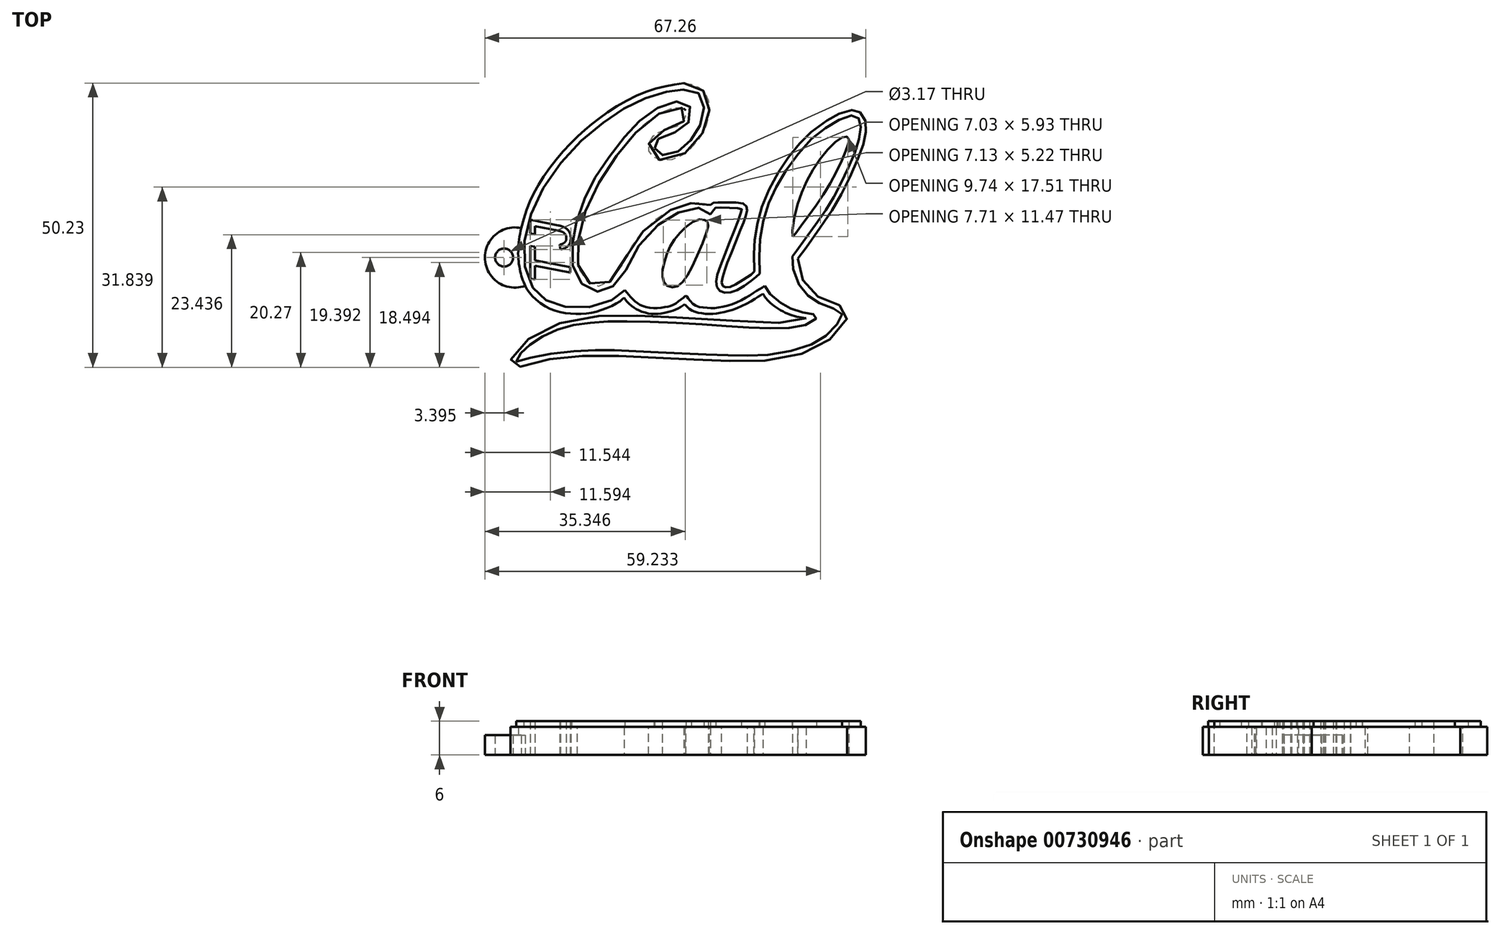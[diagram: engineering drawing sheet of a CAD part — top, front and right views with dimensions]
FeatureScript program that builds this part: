
annotation { "Feature Type Name" : "Feature", "Feature Type Description" : "" }
export const myFeature = defineFeature(function(context is Context, id is Id, definition is map)
    precondition{}
    {
        {
            var Q0;
            Q0=qCreatedBy(makeId("Top.planeOp"),FACE);
            var sketch = newSketch(context, id + "F0", { "sketchPlane" : qUnion([Q0])});
            skFitSpline(sketch, "E0", {"points": [v(-4.7, 24.02) * mm, v(-9.21, 23.15) * mm, v(-14.3, 21.16) * mm, v(-19.5, 17.88) * mm, v(-22.84, 15.12) * mm, v(-26.76, 11.1) * mm, v(-29.99, 6.61) * mm, v(-32.03, 2.73) * mm, v(-33.4, -1.61) * mm, v(-33.93, -5.95) * mm, v(-33.53, -9.41) * mm, v(-32.68, -11.82) * mm, v(-31.5, -13.58) * mm, v(-28.51, -15.76) * mm, v(-25.22, -16.67) * mm, v(-21.85, -16.67) * mm, v(-18.53, -15.85) * mm, v(-15.8, -14.43) * mm, v(-15.24, -13.92) * mm], "startDerivative": vector(-73.34, -11.53) * mm, "endDerivative": vector(17.37, 18.62) * mm});
            skFitSpline(sketch, "E1", {"points": [v(-4.7, 24.02) * mm, v(-3.12, 23.72) * mm, v(-1.32, 22.73) * mm, v(-0.4, 21.1) * mm, v(-0.19, 19.64) * mm, v(-0.46, 17.5) * mm, v(-1.34, 15.24) * mm, v(-3, 12.9) * mm, v(-5.25, 11.12) * mm, v(-8.18, 10.3) * mm, v(-10.22, 11.1) * mm, v(-10.93, 12.5) * mm, v(-10.4, 14.33) * mm, v(-9.18, 15.29) * mm, v(-7.2, 15.98) * mm, v(-5.28, 16.76) * mm, v(-4.46, 17.73) * mm, v(-4.35, 19.05) * mm, v(-4.7, 19.49) * mm, v(-5.77, 19.74) * mm, v(-8.08, 19.08) * mm, v(-10.95, 17.28) * mm, v(-13.73, 14.65) * mm, v(-15.92, 11.97) * mm, v(-18.22, 8.83) * mm, v(-20.42, 5.07) * mm, v(-22.03, 1.43) * mm, v(-22.95, -1.6) * mm, v(-23.43, -5.01) * mm, v(-23.44, -7.42) * mm, v(-22.82, -9.67) * mm, v(-21.67, -11.12) * mm, v(-20.22, -11.83) * mm, v(-18.54, -11.59) * mm, v(-16.3, -9.45) * mm, v(-14.2, -5.42) * mm, v(-12.55, -2.99) * mm, v(-9.6, 0) * mm, v(-5.75, 2.15) * mm, v(-4.7, 2.5) * mm, v(-2.6, 2.9) * mm, v(-0.85, 2.81) * mm, v(0, 2.46) * mm], "startDerivative": vector(77.61, -10.14) * mm, "endDerivative": vector(51.5, -26.92) * mm});
            skFitSpline(sketch, "E2", {"points": [v(0, 2.46) * mm, v(0.28, 2.72) * mm, v(0.87, 2.9) * mm, v(2.4, 2.94) * mm, v(5.4, 2.83) * mm, v(6.2, 2.46) * mm, v(6.5, 1.89) * mm, v(6.5, 1.4) * mm, v(6.07, 0) * mm, v(5.35, -1.82) * mm, v(3.47, -6.54) * mm, v(2.55, -9.02) * mm, v(2.07, -10.65) * mm, v(2.04, -11.5) * mm, v(2.25, -11.9) * mm, v(2.52, -12.02) * mm, v(2.9, -12.1) * mm, v(3.58, -12) * mm, v(5, -11.26) * mm, v(7.38, -9.65) * mm, v(7.75, -9.28) * mm], "startDerivative": vector(8.73, 10) * mm, "endDerivative": vector(7.71, 9.34) * mm});
            skFitSpline(sketch, "E3", {"points": [v(7.75, -9.28) * mm, v(7.67, -6.17) * mm, v(7.75, -4.22) * mm, v(8.16, -1.42) * mm, v(8.86, 1.43) * mm, v(10.07, 4.56) * mm, v(11.9, 8.03) * mm, v(13.77, 10.86) * mm, v(15.67, 13.23) * mm, v(17.5, 15.1) * mm, v(20.59, 17.4) * mm, v(22.34, 18.43) * mm, v(24.19, 19.11) * mm, v(25.4, 19.25) * mm, v(26.1, 19.05) * mm, v(26.66, 18.64) * mm, v(27.28, 17.6) * mm, v(27.44, 16.52) * mm, v(27.4, 15.04) * mm, v(27.06, 13.35) * mm, v(26.43, 11.57) * mm, v(24.97, 8.1) * mm, v(23.3, 4.7) * mm, v(21.54, 1.6) * mm, v(18.9, -2.23) * mm, v(15.96, -6.32) * mm, v(15.47, -6.98) * mm], "startDerivative": vector(-2.8, 76.12) * mm, "endDerivative": vector(-16.99, -22) * mm});
            skFitSpline(sketch, "E4", {"points": [v(15.47, -6.98) * mm, v(15.47, -8.07) * mm, v(15.9, -9.84) * mm, v(16.65, -11.36) * mm, v(17.4, -12.33) * mm, v(18.9, -13.64) * mm, v(20.59, -14.36) * mm, v(22.36, -15.03) * mm, v(23.17, -15.48) * mm, v(23.92, -16.1) * mm, v(24.16, -17.1) * mm, v(24.02, -17.86) * mm, v(23.06, -19.38) * mm, v(20.9, -21.42) * mm, v(18.38, -22.95) * mm, v(15.02, -24.15) * mm, v(10.48, -24.94) * mm, v(6.7, -25.1) * mm, v(2.6, -25.05) * mm, v(-1.8, -24.88) * mm, v(-4.7, -24.77) * mm, v(-10.38, -24.47) * mm, v(-14.79, -24.26) * mm, v(-18.25, -24.15) * mm, v(-22.76, -24.23) * mm, v(-26.47, -24.5) * mm, v(-29.37, -25) * mm, v(-32.67, -25.83) * mm, v(-34.12, -26.19) * mm, v(-34.7, -26.14) * mm, v(-35.17, -25.7) * mm, v(-35.28, -25.12) * mm, v(-34.94, -24.15) * mm, v(-33.62, -22.44) * mm, v(-30.22, -20.02) * mm, v(-26.9, -18.52) * mm, v(-21.96, -17.34) * mm, v(-17.65, -17.1) * mm, v(-12.83, -17.1) * mm, v(-8.42, -17.27) * mm, v(-0.45, -17.68) * mm, v(9.32, -18.29) * mm, v(13.39, -18.32) * mm, v(16.5, -17.78) * mm, v(16.89, -17.55) * mm], "startDerivative": vector(-4.14, -70.71) * mm, "endDerivative": vector(29.82, 23.88) * mm});
            skFitSpline(sketch, "E5", {"points": [v(16.89, -17.55) * mm, v(14.28, -16.98) * mm, v(11.54, -15.58) * mm, v(9.76, -13.96) * mm, v(9.29, -13.24) * mm], "startDerivative": vector(-9.33, 1.49) * mm, "endDerivative": vector(-2.3, 4.22) * mm});
            skFitSpline(sketch, "E6", {"points": [v(9.29, -13.24) * mm, v(8.22, -13.9) * mm, v(4.92, -15.68) * mm, v(2.04, -16.52) * mm, v(0, -16.77) * mm, v(-2.04, -16.59) * mm, v(-3.52, -16.02) * mm, v(-4.42, -15.2) * mm, v(-4.52, -15.03) * mm], "startDerivative": vector(-8.4, -5.18) * mm, "endDerivative": vector(-1.48, 3.32) * mm});
            skFitSpline(sketch, "E7", {"points": [v(-4.52, -15.03) * mm, v(-5.36, -15.63) * mm, v(-6.48, -16.16) * mm, v(-7.6, -16.5) * mm, v(-9.27, -16.78) * mm, v(-10.84, -16.7) * mm, v(-12.41, -16.24) * mm, v(-13.51, -15.66) * mm, v(-14.61, -14.7) * mm, v(-15.24, -13.92) * mm], "startDerivative": vector(-8.04, -6.35) * mm, "endDerivative": vector(-5.78, 7.96) * mm});
            skFitSpline(sketch, "E8", {"points": [v(-1.42, -1.1) * mm, v(-2.1, -1.17) * mm, v(-3.9, -2.27) * mm, v(-5.53, -4.08) * mm, v(-7, -7.2) * mm, v(-7.51, -9.93) * mm, v(-7.17, -10.91) * mm, v(-6.4, -11.13) * mm, v(-5.15, -9.95) * mm, v(-3.46, -6.62) * mm, v(-1.58, -2.01) * mm, v(-1.42, -1.1) * mm]});
            skFitSpline(sketch, "E9", {"points": [v(23.12, 13.02) * mm, v(21.35, 11.17) * mm, v(18.38, 7) * mm, v(16.22, 1.63) * mm, v(15.86, 0) * mm], "startDerivative": vector(-7.9, -7.88) * mm, "endDerivative": vector(-1.4, -8.04) * mm});
            skFitSpline(sketch, "E10", {"points": [v(15.86, 0) * mm, v(17.9, 3.15) * mm, v(21.27, 8.73) * mm, v(23.12, 13.02) * mm], "startDerivative": vector(6.41, 9.86) * mm, "endDerivative": vector(4.78, 12.62) * mm});
            skFitSpline(sketch, "E11", {"points": [v(-9.86, 12.47) * mm, v(-9.34, 11.59) * mm, v(-7.53, 11.3) * mm, v(-4.88, 12.43) * mm, v(-3, 14.56) * mm, v(-1.52, 17.36) * mm, v(-1.23, 20.65) * mm, v(-2.4, 22.42) * mm, v(-5, 22.86) * mm, v(-7.9, 22.46) * mm, v(-12.87, 20.77) * mm, v(-17.92, 17.77) * mm, v(-24.06, 12.6) * mm, v(-29.75, 5.05) * mm, v(-32.6, -2.45) * mm, v(-32.6, -9.1) * mm, v(-30.51, -13.2) * mm, v(-27.7, -14.96) * mm, v(-22.61, -15.72) * mm, v(-17.24, -14.24) * mm, v(-15.07, -12.6) * mm], "startDerivative": vector(13.93, -39.77) * mm, "endDerivative": vector(44.74, 41.56) * mm});
            skFitSpline(sketch, "E12", {"points": [v(-9.86, 12.47) * mm, v(-9.86, 13.43) * mm, v(-8.93, 14.32) * mm, v(-6.29, 15.32) * mm, v(-4.12, 16.64) * mm, v(-3.32, 19.09) * mm, v(-4.2, 20.37) * mm, v(-6.29, 20.7) * mm, v(-9.74, 19.37) * mm, v(-13.1, 16.72) * mm, v(-16.07, 13.31) * mm, v(-19.48, 8.62) * mm, v(-21.8, 4.5) * mm, v(-23.7, -0.68) * mm, v(-24.34, -4.25) * mm, v(-24.22, -8.62) * mm, v(-22.45, -11.71) * mm, v(-20.04, -12.84) * mm, v(-17.8, -12.23) * mm, v(-15.6, -10.15) * mm, v(-12.54, -4.61) * mm, v(-7.85, 0) * mm, v(-4.04, 1.68) * mm, v(-1.03, 1.84) * mm, v(0, 0.84) * mm], "startDerivative": vector(-6.96, 44.46) * mm, "endDerivative": vector(29.41, -44.04) * mm});
            skFitSpline(sketch, "E13", {"points": [v(0, 0.84) * mm, v(0.74, 1.77) * mm, v(0.9, 1.97) * mm, v(3.26, 1.97) * mm, v(5.5, 1.74) * mm, v(5.47, 1.29) * mm, v(4.03, -2.54) * mm, v(1.42, -9.23) * mm, v(1.05, -11.56) * mm, v(1.64, -12.7) * mm, v(2.9, -13.03) * mm, v(5.02, -12.4) * mm, v(7.6, -10.62) * mm, v(8.73, -9.66) * mm], "startDerivative": vector(15.5, 18.27) * mm, "endDerivative": vector(14.9, 13.06) * mm});
            skFitSpline(sketch, "E14", {"points": [v(8.73, -9.66) * mm, v(8.73, -4.13) * mm, v(10.04, 2.14) * mm, v(12.82, 7.67) * mm, v(17.55, 13.82) * mm, v(21.98, 17.11) * mm, v(25.04, 18.3) * mm, v(26.12, 17.88) * mm, v(26.51, 16.58) * mm, v(26.17, 13.77) * mm, v(24.64, 9.71) * mm, v(22.4, 5.03) * mm, v(20.13, 1.2) * mm, v(16.65, -3.64) * mm, v(14.89, -6.11) * mm, v(14.52, -6.62) * mm], "startDerivative": vector(-3, 68.23) * mm, "endDerivative": vector(-11.63, -15.92) * mm});
            skFitSpline(sketch, "E15", {"points": [v(14.52, -6.62) * mm, v(14.52, -8.21) * mm, v(15.34, -11.1) * mm, v(16.73, -13) * mm, v(18.35, -14.42) * mm, v(20.59, -15.36) * mm, v(22.63, -16.24) * mm, v(23.23, -16.83) * mm, v(23.08, -17.48) * mm, v(21.5, -19.61) * mm, v(19.48, -21.28) * mm, v(15.54, -22.99) * mm, v(9.73, -24.04) * mm, v(5.22, -24.15) * mm, v(0.5, -24) * mm, v(-5.99, -23.7) * mm, v(-11.91, -23.41) * mm, v(-17.16, -23.18) * mm, v(-21.27, -23.21) * mm, v(-27.17, -23.67) * mm, v(-31.93, -24.57) * mm, v(-34.29, -25.23) * mm], "startDerivative": vector(-3.17, -43.77) * mm, "endDerivative": vector(-52.94, -15.63) * mm});
            skFitSpline(sketch, "E16", {"points": [v(-34.29, -25.23) * mm, v(-33.52, -23.78) * mm, v(-31.76, -22.16) * mm, v(-28.5, -20.15) * mm, v(-24.16, -18.76) * mm, v(-19.37, -18.2) * mm, v(-13.22, -18.1) * mm, v(-2.55, -18.56) * mm, v(6.55, -19.16) * mm, v(13.36, -19.3) * mm, v(17.52, -18.45) * mm, v(18.8, -17.29) * mm, v(18.43, -16.89) * mm, v(17.01, -16.63) * mm, v(14.52, -15.98) * mm, v(12.56, -14.96) * mm, v(10.4, -13.06) * mm, v(9.61, -11.84) * mm], "startDerivative": vector(15.69, 36.7) * mm, "endDerivative": vector(-16.44, 30.57) * mm});
            skFitSpline(sketch, "E17", {"points": [v(9.61, -11.84) * mm, v(8.17, -12.72) * mm, v(5.39, -14.4) * mm, v(1.79, -15.61) * mm, v(-0.74, -15.7) * mm, v(-2.95, -15.1) * mm, v(-4.09, -13.8) * mm, v(-4.28, -13.54) * mm], "startDerivative": vector(-10.4, -6.12) * mm, "endDerivative": vector(-2.9, 3.4) * mm});
            skFitSpline(sketch, "E18", {"points": [v(-4.28, -13.54) * mm, v(-4.73, -13.86) * mm, v(-6.27, -15.03) * mm, v(-7.77, -15.53) * mm, v(-10.45, -15.74) * mm, v(-12.6, -15.06) * mm, v(-13.95, -13.94) * mm, v(-15.07, -12.6) * mm], "startDerivative": vector(-4.65, -2.98) * mm, "endDerivative": vector(-7.57, 9.59) * mm});
            skFitSpline(sketch, "E19", {"points": [v(-1.03, -0.2) * mm, v(-2.1, -0.1) * mm, v(-4.28, -1.37) * mm, v(-6.26, -3.54) * mm, v(-7.55, -5.85) * mm, v(-8.33, -8.51) * mm, v(-8.43, -10.48) * mm, v(-7.94, -11.51) * mm, v(-7.2, -12) * mm, v(-5.95, -12) * mm, v(-4.63, -10.84) * mm, v(-2.83, -7.6) * mm, v(-0.55, -2.01) * mm, v(-0.43, -0.8) * mm, v(-0.72, -0.33) * mm, v(-1.03, -0.2) * mm]});
            skFitSpline(sketch, "E20", {"points": [v(14.55, -3.13) * mm, v(15.03, 1.16) * mm, v(17.55, 7.73) * mm, v(21.26, 12.86) * mm, v(23.63, 14.55) * mm, v(24.2, 14.48) * mm, v(24.47, 13.94) * mm, v(24.13, 12.62) * mm, v(22.07, 7.94) * mm, v(18.26, 1.8) * mm, v(15.03, -2.59) * mm, v(14.55, -3.13) * mm]});
            skText(sketch, "E21", { "text": "TJ", "fontName": "Arimo-Italic.ttf"});
            skPoint(sketch, "E22.endSnap0", {"position": v(5.12, 34.02) * mm});
            skArc(sketch, "E23", {"start": v(-33.4, -1.61) * mm, "mid": v(-39.8, -7.19) * mm, "end": v(-32.68, -11.82) * mm});
            skCircle(sketch, "E24", {"center": v(-36.42, -6.82) * mm, "radius": 1.59 * mm});
            const initialGuessF0  = {"E21": [-0.02475, -0.0116, 0, 1, 0.00736]};
            skSetInitialGuess(sketch, initialGuessF0);
            skSolve(sketch);
        }
        {
            var Q0;
            Q0=makeQuery(id+"F0.imprint","IMPRINT",FACE,{"disambiguationData":[TD([[makeQuery(id+"F0.imprint","IMPRINT",EDGE,{"derivedFrom":sQuery(id+"F0.wireOp",EDGE,"E11")}),1.0]])]});
            extrude(context, id + "F1", {"entities" : qUnion([Q0]), "depth" : 6 * mm, "offsetDistance" : 25 * mm});
        }
        {
            var Q0;
            Q0=makeQuery(id+"F0.imprint","IMPRINT",FACE,{"disambiguationData":[TD([[makeQuery(id+"F0.imprint","IMPRINT",EDGE,{"derivedFrom":sQuery(id+"F0.wireOp",EDGE,"E0")}),1.0]])]});
            extrude(context, id + "F2", {"entities" : qUnion([Q0]), "operationType" : NewBodyOperationType.ADD, "depth" : 5 * mm, "offsetDistance" : 25 * mm});
        }
        {
            var Q0;
            {var subQ0=sQuery(id+"F0.wireOp",EDGE,"E23");Q0=makeQuery(id+"F0.imprint","IMPRINT",FACE,{"disambiguationData":[TD([[makeQuery(id+"F0.imprint","IMPRINT",EDGE,{"derivedFrom":subQ0}),1.0]])]});}
            extrude(context, id + "F3", {"entities" : qUnion([Q0]), "operationType" : NewBodyOperationType.ADD, "depth" : 3.5 * mm, "offsetDistance" : 25 * mm});
        }
    });
